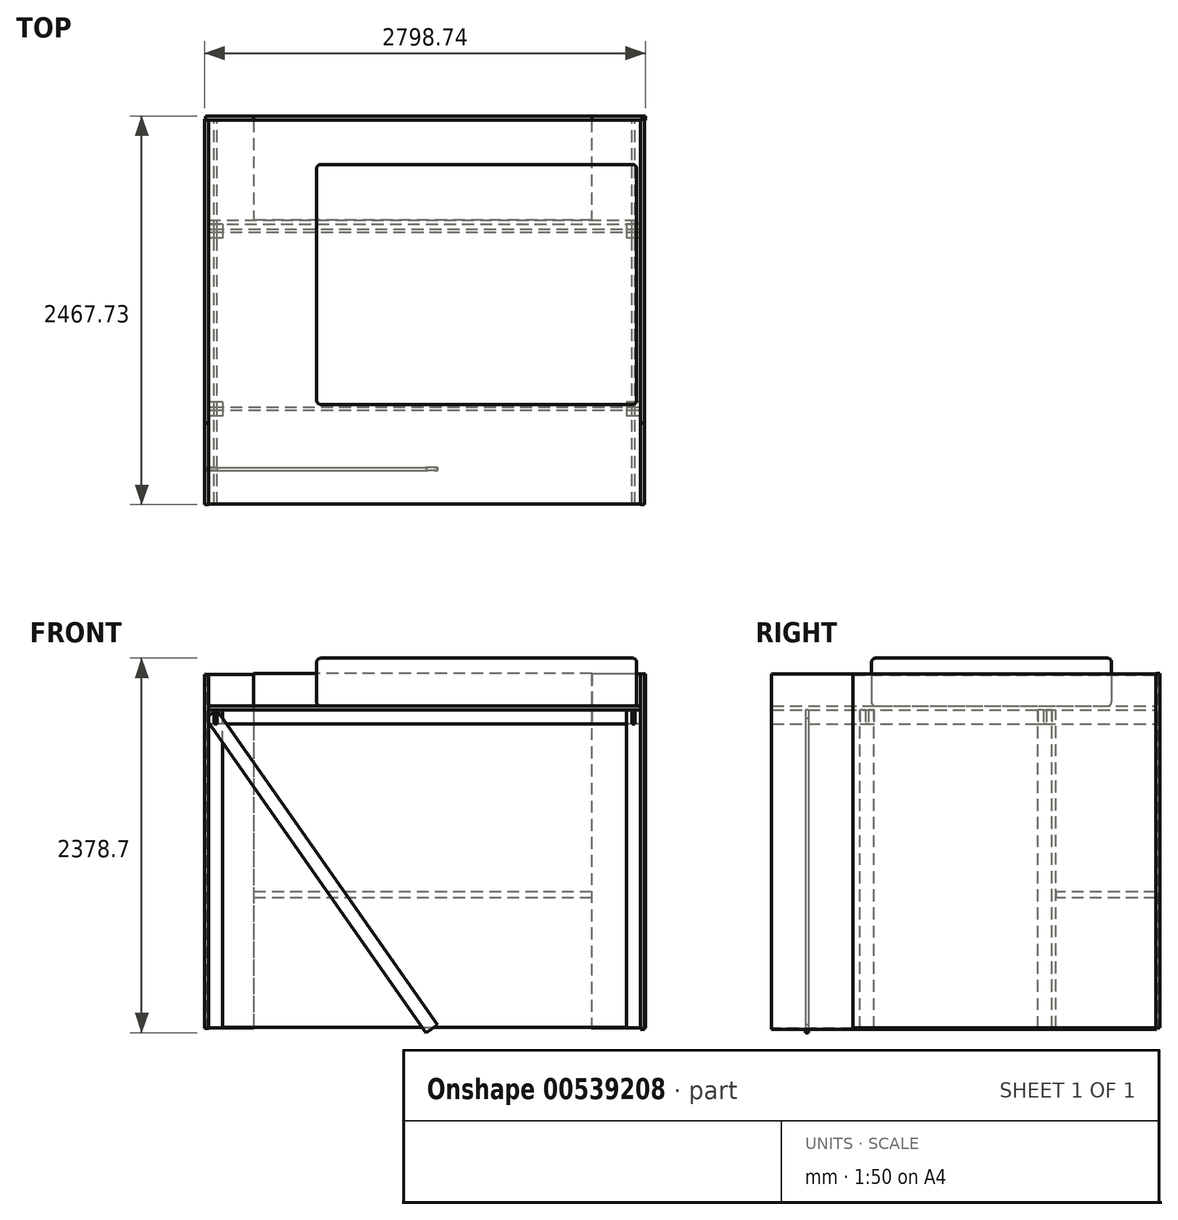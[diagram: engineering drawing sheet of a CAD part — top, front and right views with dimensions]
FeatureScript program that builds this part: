
annotation { "Feature Type Name" : "Feature", "Feature Type Description" : "" }
export const myFeature = defineFeature(function(context is Context, id is Id, definition is map)
    precondition{}
    {
        {
            var Q0;
            Q0=qCreatedBy(makeId("Top.planeOp"),FACE);
            var sketch = newSketch(context, id + "F0", { "sketchPlane" : qUnion([Q0])});
            skLineSegment(sketch, "E0.bottom", {"start": v(44.45, -44.45) * mm, "end": v(-44.45, -44.45) * mm});
            skLineSegment(sketch, "E0.top", {"start": v(44.45, 44.45) * mm, "end": v(-44.45, 44.45) * mm});
            skLineSegment(sketch, "E0.left", {"start": v(44.45, -44.45) * mm, "end": v(44.45, 44.45) * mm});
            skLineSegment(sketch, "E0.right", {"start": v(-44.45, -44.45) * mm, "end": v(-44.45, 44.45) * mm});
            skPoint(sketch, "E0.middle", {"position": v(0, 0) * mm});
            skSolve(sketch);
        }
        {
            var Q0;
            Q0=makeQuery(id+"F0.imprint","IMPRINT",FACE,{"disambiguationData":[TD([[makeQuery(id+"F0.imprint","IMPRINT",EDGE,{"derivedFrom":sQuery(id+"F0.wireOp",EDGE,"E0.bottom")}),-1.0]])]});
            extrude(context, id + "F1", {"entities" : qUnion([Q0]), "depth" : 2019.3 * mm, "offsetDistance" : 25.4 * mm});
        }
        {
            var Q0;
            Q0=qCreatedBy(makeId("Top.planeOp"),FACE);
            var sketch = newSketch(context, id + "F2", { "sketchPlane" : qUnion([Q0])});
            skLineSegment(sketch, "E1.bottom", {"start": v(9.53, 57.15) * mm, "end": v(-9.52, 57.15) * mm});
            skLineSegment(sketch, "E1.top", {"start": v(9.52, -57.15) * mm, "end": v(-9.53, -57.15) * mm});
            skLineSegment(sketch, "E1.left", {"start": v(9.53, 57.15) * mm, "end": v(9.52, -57.15) * mm});
            skLineSegment(sketch, "E1.right", {"start": v(-9.52, 57.15) * mm, "end": v(-9.53, -57.15) * mm});
            skPoint(sketch, "E1.middle", {"position": v(0, 0) * mm});
            skSolve(sketch);
        }
        {
            var Q0;
            Q0 = qSketchRegion(id + "F2", true);
            extrude(context, id + "F3", {"entities" : qUnion([Q0]), "operationType" : NewBodyOperationType.REMOVE, "oppositeDirection" : true, "depth" : -88.9 * mm, "offsetDistance" : 25.4 * mm});
        }
        {
            var Q0;
            Q0=qCreatedBy(makeId("Top.planeOp"),FACE);
            var sketch = newSketch(context, id + "F4", { "sketchPlane" : qUnion([Q0])});
            skLineSegment(sketch, "E2.bottom", {"start": v(58.89, 9.53) * mm, "end": v(-55.41, 9.52) * mm});
            skLineSegment(sketch, "E2.top", {"start": v(58.89, -9.52) * mm, "end": v(-55.41, -9.53) * mm});
            skLineSegment(sketch, "E2.left", {"start": v(58.89, 9.53) * mm, "end": v(58.89, -9.52) * mm});
            skLineSegment(sketch, "E2.right", {"start": v(-55.41, 9.52) * mm, "end": v(-55.41, -9.53) * mm});
            skPoint(sketch, "E2.middle", {"position": v(1.74, 0) * mm});
            skSolve(sketch);
        }
        {
            var Q0;
            Q0=makeQuery(id+"F4.imprint","IMPRINT",FACE,{"disambiguationData":[TD([[makeQuery(id+"F4.imprint","IMPRINT",EDGE,{"derivedFrom":sQuery(id+"F4.wireOp",EDGE,"E2.bottom")}),1.0]])]});
            extrude(context, id + "F5", {"entities" : qUnion([Q0]), "operationType" : NewBodyOperationType.REMOVE, "oppositeDirection" : true, "depth" : -88.9 * mm, "offsetDistance" : 25.4 * mm});
        }
        {
            var Q0;
            Q0=makeQuery(id+"F1.opExtrude","SWEPT_BODY",BODY,{"disambiguationData":[OSD([sQuery(id+"F0.wireOp",EDGE,"E0.bottom"),sQuery(id+"F0.wireOp",EDGE,"E0.top"),sQuery(id+"F0.wireOp",EDGE,"E0.left"),sQuery(id+"F0.wireOp",EDGE,"E0.right")])]});
            var Q1;
            Q1=sQuery(id+"F0.wireOp",EDGE,"E0.top");
            transform(context, id + "F6", {"entities" : qUnion([Q0]), "transformType" : TransformType.ROTATION, "transformAxis" : qUnion([Q1]), "angle" : 180 * degree, "makeCopy" : false});
        }
        {
            var Q0;
            Q0=makeQuery(id+"F1.opExtrude","SWEPT_BODY",BODY,{"disambiguationData":[OSD([sQuery(id+"F0.wireOp",EDGE,"E0.bottom"),sQuery(id+"F0.wireOp",EDGE,"E0.top"),sQuery(id+"F0.wireOp",EDGE,"E0.left"),sQuery(id+"F0.wireOp",EDGE,"E0.right")])]});
            var Q1;
            Q1=makeQuery(id+"F1.opExtrude","CAP_EDGE",EDGE,{"disambiguationData":[OSD([sQuery(id+"F0.wireOp",EDGE,"E0.top")])],"isStart":false});
            transform(context, id + "F7", {"entities" : qUnion([Q0]), "transformType" : TransformType.TRANSLATION_DISTANCE, "transformDirection" : qUnion([Q1]), "distance" : 914.4 * mm, "makeCopy" : false});
        }
        {
            var Q0;
            Q0=makeQuery(id+"F1.opExtrude","SWEPT_BODY",BODY,{"disambiguationData":[OSD([sQuery(id+"F0.wireOp",EDGE,"E0.bottom"),sQuery(id+"F0.wireOp",EDGE,"E0.top"),sQuery(id+"F0.wireOp",EDGE,"E0.left"),sQuery(id+"F0.wireOp",EDGE,"E0.right")])]});
            transform(context, id + "F8", {"entities" : qUnion([Q0]), "transformType" : TransformType.TRANSLATION_3D, "dx" : 1828.8 * mm, "dy" : 0 * mm, "dz" : 0 * mm, "makeCopy" : true});
        }
        {
            var Q0;
            Q0=makeQuery(id+"F1.opExtrude","SWEPT_BODY",BODY,{"disambiguationData":[OSD([sQuery(id+"F0.wireOp",EDGE,"E0.bottom"),sQuery(id+"F0.wireOp",EDGE,"E0.top"),sQuery(id+"F0.wireOp",EDGE,"E0.left"),sQuery(id+"F0.wireOp",EDGE,"E0.right")])]});
            var Q1;
            Q1=makeQuery(id+"F8.opPattern","COPY",BODY,{"derivedFrom":makeQuery(id+"F1.opExtrude","SWEPT_BODY",BODY,{"disambiguationData":[OSD([sQuery(id+"F0.wireOp",EDGE,"E0.bottom"),sQuery(id+"F0.wireOp",EDGE,"E0.top"),sQuery(id+"F0.wireOp",EDGE,"E0.left"),sQuery(id+"F0.wireOp",EDGE,"E0.right")])]}),"instanceName":"1"});
            transform(context, id + "F9", {"entities" : qUnion([Q0, Q1]), "transformType" : TransformType.TRANSLATION_3D, "dx" : 0 * mm, "dy" : 762 * mm, "dz" : 0 * mm, "makeCopy" : false});
        }
        {
            var Q0;
            Q0=makeQuery(id+"F8.opPattern","COPY",BODY,{"derivedFrom":makeQuery(id+"F1.opExtrude","SWEPT_BODY",BODY,{"disambiguationData":[OSD([sQuery(id+"F0.wireOp",EDGE,"E0.bottom"),sQuery(id+"F0.wireOp",EDGE,"E0.top"),sQuery(id+"F0.wireOp",EDGE,"E0.left"),sQuery(id+"F0.wireOp",EDGE,"E0.right")])]}),"instanceName":"1"});
            transform(context, id + "F10", {"entities" : qUnion([Q0]), "transformType" : TransformType.TRANSLATION_3D, "dx" : 0 * mm, "dy" : -1524 * mm, "dz" : 0 * mm, "makeCopy" : true});
        }
        {
            var Q0;
            Q0=makeQuery(id+"F1.opExtrude","SWEPT_BODY",BODY,{"disambiguationData":[OSD([sQuery(id+"F0.wireOp",EDGE,"E0.bottom"),sQuery(id+"F0.wireOp",EDGE,"E0.top"),sQuery(id+"F0.wireOp",EDGE,"E0.left"),sQuery(id+"F0.wireOp",EDGE,"E0.right")])]});
            transform(context, id + "F11", {"entities" : qUnion([Q0]), "transformType" : TransformType.TRANSLATION_3D, "dx" : 0 * mm, "dy" : -1524 * mm, "dz" : 0 * mm, "makeCopy" : true});
        }
        {
            var Q0;
            Q0=qCreatedBy(makeId("Top.planeOp"),FACE);
            var sketch = newSketch(context, id + "F12", { "sketchPlane" : qUnion([Q0])});
            skLineSegment(sketch, "E3.bottom", {"start": v(-1219.2, -1371.6) * mm, "end": v(1219.2, -1371.6) * mm});
            skLineSegment(sketch, "E3.top", {"start": v(-1219.2, 1371.6) * mm, "end": v(1219.2, 1371.6) * mm});
            skLineSegment(sketch, "E3.left", {"start": v(-1219.2, -1371.6) * mm, "end": v(-1219.2, 1371.6) * mm});
            skLineSegment(sketch, "E3.right", {"start": v(1219.2, -1371.6) * mm, "end": v(1219.2, 1371.6) * mm});
            skPoint(sketch, "E3.middle", {"position": v(0, 0) * mm});
            skSolve(sketch);
        }
        {
            var Q0;
            Q0=makeQuery(id+"F12.imprint","IMPRINT",FACE,{"disambiguationData":[TD([[makeQuery(id+"F12.imprint","IMPRINT",EDGE,{"derivedFrom":sQuery(id+"F12.wireOp",EDGE,"E3.bottom")}),1.0]])]});
            extrude(context, id + "F13", {"entities" : qUnion([Q0]), "depth" : 25.4 * mm, "offsetDistance" : 25.4 * mm});
        }
        {
            var Q0;
            Q0=makeQuery(id+"F13.opExtrude","SWEPT_BODY",BODY,{"disambiguationData":[OSD([sQuery(id+"F12.wireOp",EDGE,"E3.bottom"),sQuery(id+"F12.wireOp",EDGE,"E3.top"),sQuery(id+"F12.wireOp",EDGE,"E3.left"),sQuery(id+"F12.wireOp",EDGE,"E3.right")])]});
            var Q1;
            Q1=makeQuery(id+"F11.opPattern","COPY",EDGE,{"derivedFrom":makeQuery(id+"F1.opExtrude","SWEPT_EDGE",EDGE,{"disambiguationData":[OSD([sQuery(id+"F0.wireOp",EDGE,"E0.top"),sQuery(id+"F0.wireOp",EDGE,"E0.right")])]}),"instanceName":"1"});
            transform(context, id + "F14", {"entities" : qUnion([Q0]), "transformType" : TransformType.ROTATION, "transformAxis" : qUnion([Q1]), "angle" : 90 * degree, "makeCopy" : false});
        }
        {
            var Q0;
            Q0=makeQuery(id+"F13.opExtrude","SWEPT_BODY",BODY,{"disambiguationData":[OSD([sQuery(id+"F12.wireOp",EDGE,"E3.bottom"),sQuery(id+"F12.wireOp",EDGE,"E3.top"),sQuery(id+"F12.wireOp",EDGE,"E3.left"),sQuery(id+"F12.wireOp",EDGE,"E3.right")])]});
            transform(context, id + "F15", {"entities" : qUnion([Q0]), "transformType" : TransformType.TRANSLATION_3D, "dx" : 1625.6 * mm, "dy" : -76.2 * mm, "dz" : 0 * mm, "makeCopy" : false});
        }
        {
            var Q0;
            Q0=makeQuery(id+"F11.opPattern","COPY",BODY,{"derivedFrom":makeQuery(id+"F1.opExtrude","SWEPT_BODY",BODY,{"disambiguationData":[OSD([sQuery(id+"F0.wireOp",EDGE,"E0.bottom"),sQuery(id+"F0.wireOp",EDGE,"E0.top"),sQuery(id+"F0.wireOp",EDGE,"E0.left"),sQuery(id+"F0.wireOp",EDGE,"E0.right")])]}),"instanceName":"1"});
            transform(context, id + "F16", {"entities" : qUnion([Q0]), "transformType" : TransformType.TRANSLATION_3D, "dx" : -196.85 * mm, "dy" : 0 * mm, "dz" : 0 * mm, "makeCopy" : false});
        }
        {
            var Q0;
            Q0=makeQuery(id+"F1.opExtrude","SWEPT_BODY",BODY,{"disambiguationData":[OSD([sQuery(id+"F0.wireOp",EDGE,"E0.bottom"),sQuery(id+"F0.wireOp",EDGE,"E0.top"),sQuery(id+"F0.wireOp",EDGE,"E0.left"),sQuery(id+"F0.wireOp",EDGE,"E0.right")])]});
            transform(context, id + "F17", {"entities" : qUnion([Q0]), "transformType" : TransformType.TRANSLATION_3D, "dx" : -196.85 * mm, "dy" : 0 * mm, "dz" : 0 * mm, "makeCopy" : false});
        }
        {
            var Q0;
            Q0=makeQuery(id+"F8.opPattern","COPY",BODY,{"derivedFrom":makeQuery(id+"F1.opExtrude","SWEPT_BODY",BODY,{"disambiguationData":[OSD([sQuery(id+"F0.wireOp",EDGE,"E0.bottom"),sQuery(id+"F0.wireOp",EDGE,"E0.top"),sQuery(id+"F0.wireOp",EDGE,"E0.left"),sQuery(id+"F0.wireOp",EDGE,"E0.right")])]}),"instanceName":"1"});
            var Q1;
            Q1=makeQuery(id+"F10.opPattern","COPY",BODY,{"derivedFrom":makeQuery(id+"F8.opPattern","COPY",BODY,{"derivedFrom":makeQuery(id+"F1.opExtrude","SWEPT_BODY",BODY,{"disambiguationData":[OSD([sQuery(id+"F0.wireOp",EDGE,"E0.bottom"),sQuery(id+"F0.wireOp",EDGE,"E0.top"),sQuery(id+"F0.wireOp",EDGE,"E0.left"),sQuery(id+"F0.wireOp",EDGE,"E0.right")])]}),"instanceName":"1"}),"instanceName":"1"});
            transform(context, id + "F18", {"entities" : qUnion([Q0, Q1]), "transformType" : TransformType.TRANSLATION_3D, "dx" : 196.85 * mm, "dy" : 0 * mm, "dz" : 0 * mm, "makeCopy" : false});
        }
        {
            var Q0;
            Q0=makeQuery(id+"F13.opExtrude","SWEPT_BODY",BODY,{"disambiguationData":[OSD([sQuery(id+"F12.wireOp",EDGE,"E3.bottom"),sQuery(id+"F12.wireOp",EDGE,"E3.top"),sQuery(id+"F12.wireOp",EDGE,"E3.left"),sQuery(id+"F12.wireOp",EDGE,"E3.right")])]});
            transform(context, id + "F19", {"entities" : qUnion([Q0]), "transformType" : TransformType.TRANSLATION_3D, "dx" : 63.5 * mm, "dy" : 0 * mm, "dz" : 0 * mm, "makeCopy" : false});
        }
        {
            var Q0;
            Q0=makeQuery(id+"F13.opExtrude","SWEPT_BODY",BODY,{"disambiguationData":[OSD([sQuery(id+"F12.wireOp",EDGE,"E3.bottom"),sQuery(id+"F12.wireOp",EDGE,"E3.top"),sQuery(id+"F12.wireOp",EDGE,"E3.left"),sQuery(id+"F12.wireOp",EDGE,"E3.right")])]});
            transform(context, id + "F20", {"entities" : qUnion([Q0]), "transformType" : TransformType.TRANSLATION_3D, "dx" : 0 * mm, "dy" : -50.8 * mm, "dz" : 0 * mm, "makeCopy" : false});
        }
        {
            var Q0;
            Q0=makeQuery(id+"F1.opExtrude","SWEPT_BODY",BODY,{"disambiguationData":[OSD([sQuery(id+"F0.wireOp",EDGE,"E0.bottom"),sQuery(id+"F0.wireOp",EDGE,"E0.top"),sQuery(id+"F0.wireOp",EDGE,"E0.left"),sQuery(id+"F0.wireOp",EDGE,"E0.right")])]});
            var Q1;
            Q1=makeQuery(id+"F11.opPattern","COPY",BODY,{"derivedFrom":makeQuery(id+"F1.opExtrude","SWEPT_BODY",BODY,{"disambiguationData":[OSD([sQuery(id+"F0.wireOp",EDGE,"E0.bottom"),sQuery(id+"F0.wireOp",EDGE,"E0.top"),sQuery(id+"F0.wireOp",EDGE,"E0.left"),sQuery(id+"F0.wireOp",EDGE,"E0.right")])]}),"instanceName":"1"});
            transform(context, id + "F21", {"entities" : qUnion([Q0, Q1]), "transformType" : TransformType.TRANSLATION_3D, "dx" : -6.35 * mm, "dy" : 0 * mm, "dz" : 0 * mm, "makeCopy" : false});
        }
        {
            var Q0;
            Q0=makeQuery(id+"F8.opPattern","COPY",BODY,{"derivedFrom":makeQuery(id+"F1.opExtrude","SWEPT_BODY",BODY,{"disambiguationData":[OSD([sQuery(id+"F0.wireOp",EDGE,"E0.bottom"),sQuery(id+"F0.wireOp",EDGE,"E0.top"),sQuery(id+"F0.wireOp",EDGE,"E0.left"),sQuery(id+"F0.wireOp",EDGE,"E0.right")])]}),"instanceName":"1"});
            var Q1;
            Q1=makeQuery(id+"F10.opPattern","COPY",BODY,{"derivedFrom":makeQuery(id+"F8.opPattern","COPY",BODY,{"derivedFrom":makeQuery(id+"F1.opExtrude","SWEPT_BODY",BODY,{"disambiguationData":[OSD([sQuery(id+"F0.wireOp",EDGE,"E0.bottom"),sQuery(id+"F0.wireOp",EDGE,"E0.top"),sQuery(id+"F0.wireOp",EDGE,"E0.left"),sQuery(id+"F0.wireOp",EDGE,"E0.right")])]}),"instanceName":"1"}),"instanceName":"1"});
            transform(context, id + "F22", {"entities" : qUnion([Q0, Q1]), "transformType" : TransformType.TRANSLATION_3D, "dx" : 6.35 * mm, "dy" : 0 * mm, "dz" : 0 * mm, "makeCopy" : false});
        }
        {
            var Q0;
            Q0=qCreatedBy(makeId("Top.planeOp"),FACE);
            var sketch = newSketch(context, id + "F23", { "sketchPlane" : qUnion([Q0])});
            skLineSegment(sketch, "E4.bottom", {"start": v(1073.15, 317.5) * mm, "end": v(-1073.15, 317.5) * mm});
            skLineSegment(sketch, "E4.top", {"start": v(1073.15, -317.5) * mm, "end": v(-1073.15, -317.5) * mm});
            skLineSegment(sketch, "E4.left", {"start": v(1073.15, 317.5) * mm, "end": v(1073.15, -317.5) * mm});
            skLineSegment(sketch, "E4.right", {"start": v(-1073.15, 317.5) * mm, "end": v(-1073.15, -317.5) * mm});
            skPoint(sketch, "E4.middle", {"position": v(0, 0) * mm});
            skSolve(sketch);
        }
        {
            var Q0;
            Q0=makeQuery(id+"F23.imprint","IMPRINT",FACE,{"disambiguationData":[TD([[makeQuery(id+"F23.imprint","IMPRINT",EDGE,{"derivedFrom":sQuery(id+"F23.wireOp",EDGE,"E4.bottom")}),1.0]])]});
            extrude(context, id + "F24", {"entities" : qUnion([Q0]), "depth" : 38.1 * mm, "offsetDistance" : 25.4 * mm});
        }
        {
            var Q0;
            Q0=makeQuery(id+"F24.opExtrude","SWEPT_BODY",BODY,{"disambiguationData":[OSD([sQuery(id+"F23.wireOp",EDGE,"E4.bottom"),sQuery(id+"F23.wireOp",EDGE,"E4.top"),sQuery(id+"F23.wireOp",EDGE,"E4.left"),sQuery(id+"F23.wireOp",EDGE,"E4.right")])]});
            transform(context, id + "F25", {"entities" : qUnion([Q0]), "transformType" : TransformType.TRANSLATION_3D, "dx" : 0 * mm, "dy" : 0 * mm, "dz" : -1193.8 * mm, "makeCopy" : false});
        }
        {
            var Q0;
            Q0=makeQuery(id+"F24.opExtrude","SWEPT_BODY",BODY,{"disambiguationData":[OSD([sQuery(id+"F23.wireOp",EDGE,"E4.bottom"),sQuery(id+"F23.wireOp",EDGE,"E4.top"),sQuery(id+"F23.wireOp",EDGE,"E4.left"),sQuery(id+"F23.wireOp",EDGE,"E4.right")])]});
            transform(context, id + "F26", {"entities" : qUnion([Q0]), "transformType" : TransformType.TRANSLATION_3D, "dx" : 0 * mm, "dy" : 1016 * mm, "dz" : 0 * mm, "makeCopy" : false});
        }
        {
            var Q0;
            Q0=qCreatedBy(makeId("Front.planeOp"),FACE);
            var sketch = newSketch(context, id + "F27", { "sketchPlane" : qUnion([Q0])});
            skLineSegment(sketch, "E5.bottom", {"start": v(-1261, -20.47) * mm, "end": v(-1241.95, -20.47) * mm});
            skLineSegment(sketch, "E5.top", {"start": v(-1261, -109.37) * mm, "end": v(-1241.95, -109.37) * mm});
            skLineSegment(sketch, "E5.left", {"start": v(-1261, -20.47) * mm, "end": v(-1261, -109.37) * mm});
            skLineSegment(sketch, "E5.right", {"start": v(-1241.95, -20.47) * mm, "end": v(-1241.95, -109.37) * mm});
            skSolve(sketch);
        }
        {
            var Q0;
            Q0 = qSketchRegion(id + "F27", true);
            extrude(context, id + "F28", {"entities" : qUnion([Q0]), "depth" : 2438.4 * mm, "offsetDistance" : 25.4 * mm});
        }
        {
            var Q0;
            Q0=makeQuery(id+"F28.opExtrude","SWEPT_BODY",BODY,{"disambiguationData":[OSD([sQuery(id+"F27.wireOp",EDGE,"E5.bottom"),sQuery(id+"F27.wireOp",EDGE,"E5.top"),sQuery(id+"F27.wireOp",EDGE,"E5.left"),sQuery(id+"F27.wireOp",EDGE,"E5.right")])]});
            transform(context, id + "F29", {"entities" : qUnion([Q0]), "transformType" : TransformType.TRANSLATION_3D, "dx" : 0 * mm, "dy" : 1219.2 * mm, "dz" : 0 * mm, "makeCopy" : false});
        }
        {
            var Q0;
            Q0=makeQuery(id+"F28.opExtrude","SWEPT_BODY",BODY,{"disambiguationData":[OSD([sQuery(id+"F27.wireOp",EDGE,"E5.bottom"),sQuery(id+"F27.wireOp",EDGE,"E5.top"),sQuery(id+"F27.wireOp",EDGE,"E5.left"),sQuery(id+"F27.wireOp",EDGE,"E5.right")])]});
            transform(context, id + "F30", {"entities" : qUnion([Q0]), "transformType" : TransformType.TRANSLATION_3D, "dx" : 0 * mm, "dy" : 114.3 * mm, "dz" : 0 * mm, "makeCopy" : false});
        }
        {
            var Q0;
            Q0=makeQuery(id+"F28.opExtrude","SWEPT_BODY",BODY,{"disambiguationData":[OSD([sQuery(id+"F27.wireOp",EDGE,"E5.bottom"),sQuery(id+"F27.wireOp",EDGE,"E5.top"),sQuery(id+"F27.wireOp",EDGE,"E5.left"),sQuery(id+"F27.wireOp",EDGE,"E5.right")])]});
            transform(context, id + "F31", {"entities" : qUnion([Q0]), "transformType" : TransformType.TRANSLATION_3D, "dx" : 0 * mm, "dy" : 0 * mm, "dz" : 20.32 * mm, "makeCopy" : false});
        }
        {
            var Q0;
            Q0=makeQuery(id+"F28.opExtrude","SWEPT_BODY",BODY,{"disambiguationData":[OSD([sQuery(id+"F27.wireOp",EDGE,"E5.bottom"),sQuery(id+"F27.wireOp",EDGE,"E5.top"),sQuery(id+"F27.wireOp",EDGE,"E5.left"),sQuery(id+"F27.wireOp",EDGE,"E5.right")])]});
            transform(context, id + "F32", {"entities" : qUnion([Q0]), "transformType" : TransformType.TRANSLATION_3D, "dx" : 133.88 * mm, "dy" : 0 * mm, "dz" : 0 * mm, "makeCopy" : false});
        }
        {
            var Q0;
            Q0=makeQuery(id+"F28.opExtrude","SWEPT_BODY",BODY,{"disambiguationData":[OSD([sQuery(id+"F27.wireOp",EDGE,"E5.bottom"),sQuery(id+"F27.wireOp",EDGE,"E5.top"),sQuery(id+"F27.wireOp",EDGE,"E5.left"),sQuery(id+"F27.wireOp",EDGE,"E5.right")])]});
            transform(context, id + "F33", {"entities" : qUnion([Q0]), "transformType" : TransformType.TRANSLATION_3D, "dx" : 2235.2 * mm, "dy" : 0 * mm, "dz" : 0 * mm, "makeCopy" : true});
        }
        {
            var Q0;
            Q0=makeQuery(id+"F33.opPattern","COPY",BODY,{"derivedFrom":makeQuery(id+"F28.opExtrude","SWEPT_BODY",BODY,{"disambiguationData":[OSD([sQuery(id+"F27.wireOp",EDGE,"E5.bottom"),sQuery(id+"F27.wireOp",EDGE,"E5.top"),sQuery(id+"F27.wireOp",EDGE,"E5.left"),sQuery(id+"F27.wireOp",EDGE,"E5.right")])]}),"instanceName":"1"});
            deleteBodies(context, id + "F34", {"entities" : qUnion([Q0])});
        }
        {
            var Q0;
            Q0=makeQuery(id+"F28.opExtrude","SWEPT_BODY",BODY,{"disambiguationData":[OSD([sQuery(id+"F27.wireOp",EDGE,"E5.bottom"),sQuery(id+"F27.wireOp",EDGE,"E5.top"),sQuery(id+"F27.wireOp",EDGE,"E5.left"),sQuery(id+"F27.wireOp",EDGE,"E5.right")])]});
            var Q1;
            Q1=qCreatedBy(makeId("Right.planeOp"),FACE);
            mirror(context, id + "F35", {"entities" : qUnion([Q0]), "mirrorPlane" : qUnion([Q1])});
        }
        {
            var Q0;
            Q0=qCreatedBy(makeId("Right.planeOp"),FACE);
            var sketch = newSketch(context, id + "F36", { "sketchPlane" : qUnion([Q0])});
            skLineSegment(sketch, "E6.bottom", {"start": v(840.89, 0) * mm, "end": v(859.94, 0) * mm});
            skLineSegment(sketch, "E6.top", {"start": v(840.89, -88.9) * mm, "end": v(859.94, -88.9) * mm});
            skLineSegment(sketch, "E6.left", {"start": v(840.89, 0) * mm, "end": v(840.89, -88.9) * mm});
            skLineSegment(sketch, "E6.right", {"start": v(859.94, 0) * mm, "end": v(859.94, -88.9) * mm});
            skSolve(sketch);
        }
        {
            var Q0;
            Q0 = qSketchRegion(id + "F36", true);
            extrude(context, id + "F37", {"entities" : qUnion([Q0]), "depth" : 2743.2 * mm, "offsetDistance" : 25.4 * mm});
        }
        {
            var Q0;
            Q0=makeQuery(id+"F37.opExtrude","SWEPT_BODY",BODY,{"disambiguationData":[OSD([sQuery(id+"F36.wireOp",EDGE,"E6.bottom"),sQuery(id+"F36.wireOp",EDGE,"E6.top"),sQuery(id+"F36.wireOp",EDGE,"E6.left"),sQuery(id+"F36.wireOp",EDGE,"E6.right")])]});
            transform(context, id + "F38", {"entities" : qUnion([Q0]), "transformType" : TransformType.TRANSLATION_3D, "dx" : -1358.9 * mm, "dy" : 0 * mm, "dz" : 0 * mm, "makeCopy" : false});
        }
        {
            var Q0;
            Q0=makeQuery(id+"F37.opExtrude","SWEPT_BODY",BODY,{"disambiguationData":[OSD([sQuery(id+"F36.wireOp",EDGE,"E6.bottom"),sQuery(id+"F36.wireOp",EDGE,"E6.top"),sQuery(id+"F36.wireOp",EDGE,"E6.left"),sQuery(id+"F36.wireOp",EDGE,"E6.right")])]});
            transform(context, id + "F39", {"entities" : qUnion([Q0]), "transformType" : TransformType.TRANSLATION_3D, "dx" : 0 * mm, "dy" : -1523.5 * mm, "dz" : 0 * mm, "makeCopy" : true});
        }
        {
            var Q0;
            Q0=makeQuery(id+"F28.opExtrude","SWEPT_BODY",BODY,{"disambiguationData":[OSD([sQuery(id+"F27.wireOp",EDGE,"E5.bottom"),sQuery(id+"F27.wireOp",EDGE,"E5.top"),sQuery(id+"F27.wireOp",EDGE,"E5.left"),sQuery(id+"F27.wireOp",EDGE,"E5.right")])]});
            transform(context, id + "F40", {"entities" : qUnion([Q0]), "transformType" : TransformType.TRANSLATION_3D, "dx" : -330.2 * mm, "dy" : 0 * mm, "dz" : 0 * mm, "makeCopy" : true});
        }
        {
            var Q0;
            Q0=makeQuery(id+"F40.opPattern","COPY",BODY,{"derivedFrom":makeQuery(id+"F28.opExtrude","SWEPT_BODY",BODY,{"disambiguationData":[OSD([sQuery(id+"F27.wireOp",EDGE,"E5.bottom"),sQuery(id+"F27.wireOp",EDGE,"E5.top"),sQuery(id+"F27.wireOp",EDGE,"E5.left"),sQuery(id+"F27.wireOp",EDGE,"E5.right")])]}),"instanceName":"1"});
            transform(context, id + "F41", {"entities" : qUnion([Q0]), "transformType" : TransformType.TRANSLATION_3D, "dx" : 0 * mm, "dy" : 422.27 * mm, "dz" : 0 * mm, "makeCopy" : false});
        }
        {
            var Q0;
            Q0=makeQuery(id+"F40.opPattern","COPY",BODY,{"derivedFrom":makeQuery(id+"F28.opExtrude","SWEPT_BODY",BODY,{"disambiguationData":[OSD([sQuery(id+"F27.wireOp",EDGE,"E5.bottom"),sQuery(id+"F27.wireOp",EDGE,"E5.top"),sQuery(id+"F27.wireOp",EDGE,"E5.left"),sQuery(id+"F27.wireOp",EDGE,"E5.right")])]}),"instanceName":"1"});
            var Q1;
            {var subQ0=sQuery(id+"F36.wireOp",EDGE,"E6.left");var subQ1=sQuery(id+"F36.wireOp",EDGE,"E6.bottom");Q1=makeQuery(id+"F71cGU53pQJ6Zgx_5.boolean.opBoolean","MERGE",EDGE,{"derivedFrom":[makeQuery(id+"F39.opPattern","COPY",EDGE,{"derivedFrom":makeQuery(id+"F37.opExtrude","SWEPT_EDGE",EDGE,{"disambiguationData":[OSD([subQ1,subQ0])]}),"instanceName":"1"}),makeQuery(id+"F71cGU53pQJ6Zgx_5.opExtrude","SWEPT_EDGE",EDGE,{"disambiguationData":[OSD([subQ1,subQ0])]})]});}
            transform(context, id + "F42", {"entities" : qUnion([Q0]), "transformType" : TransformType.ROTATION, "transformAxis" : qUnion([Q1]), "angle" : 55 * degree, "makeCopy" : false});
        }
        {
            var Q0;
            Q0=makeQuery(id+"F40.opPattern","COPY",BODY,{"derivedFrom":makeQuery(id+"F28.opExtrude","SWEPT_BODY",BODY,{"disambiguationData":[OSD([sQuery(id+"F27.wireOp",EDGE,"E5.bottom"),sQuery(id+"F27.wireOp",EDGE,"E5.top"),sQuery(id+"F27.wireOp",EDGE,"E5.left"),sQuery(id+"F27.wireOp",EDGE,"E5.right")])]}),"instanceName":"1"});
            var Q1;
            Q1=makeQuery(id+"F39.opPattern","COPY",BODY,{"derivedFrom":makeQuery(id+"F37.opExtrude","SWEPT_BODY",BODY,{"disambiguationData":[OSD([sQuery(id+"F36.wireOp",EDGE,"E6.bottom"),sQuery(id+"F36.wireOp",EDGE,"E6.top"),sQuery(id+"F36.wireOp",EDGE,"E6.left"),sQuery(id+"F36.wireOp",EDGE,"E6.right")])]}),"instanceName":"1"});
            var Q2;
            Q2=makeQuery(id+"F11.opPattern","COPY",BODY,{"derivedFrom":makeQuery(id+"F1.opExtrude","SWEPT_BODY",BODY,{"disambiguationData":[OSD([sQuery(id+"F0.wireOp",EDGE,"E0.bottom"),sQuery(id+"F0.wireOp",EDGE,"E0.top"),sQuery(id+"F0.wireOp",EDGE,"E0.left"),sQuery(id+"F0.wireOp",EDGE,"E0.right")])]}),"instanceName":"1"});
            var Q3;
            Q3=makeQuery(id+"F10.opPattern","COPY",BODY,{"derivedFrom":makeQuery(id+"F8.opPattern","COPY",BODY,{"derivedFrom":makeQuery(id+"F1.opExtrude","SWEPT_BODY",BODY,{"disambiguationData":[OSD([sQuery(id+"F0.wireOp",EDGE,"E0.bottom"),sQuery(id+"F0.wireOp",EDGE,"E0.top"),sQuery(id+"F0.wireOp",EDGE,"E0.left"),sQuery(id+"F0.wireOp",EDGE,"E0.right")])]}),"instanceName":"1"}),"instanceName":"1"});
            transform(context, id + "F43", {"entities" : qUnion([Q0, Q1, Q2, Q3]), "transformType" : TransformType.TRANSLATION_3D, "dx" : 0 * mm, "dy" : 558.8 * mm, "dz" : 0 * mm, "makeCopy" : false});
        }
        {
            var Q0;
            Q0=makeQuery(id+"F11.opPattern","COPY",BODY,{"derivedFrom":makeQuery(id+"F1.opExtrude","SWEPT_BODY",BODY,{"disambiguationData":[OSD([sQuery(id+"F0.wireOp",EDGE,"E0.bottom"),sQuery(id+"F0.wireOp",EDGE,"E0.top"),sQuery(id+"F0.wireOp",EDGE,"E0.left"),sQuery(id+"F0.wireOp",EDGE,"E0.right")])]}),"instanceName":"1"});
            transform(context, id + "F44", {"entities" : qUnion([Q0]), "transformType" : TransformType.TRANSLATION_3D, "dx" : 0 * mm, "dy" : -946.15 * mm, "dz" : 0 * mm, "makeCopy" : true});
        }
        {
            var Q0;
            Q0=makeQuery(id+"F10.opPattern","COPY",BODY,{"derivedFrom":makeQuery(id+"F8.opPattern","COPY",BODY,{"derivedFrom":makeQuery(id+"F1.opExtrude","SWEPT_BODY",BODY,{"disambiguationData":[OSD([sQuery(id+"F0.wireOp",EDGE,"E0.bottom"),sQuery(id+"F0.wireOp",EDGE,"E0.top"),sQuery(id+"F0.wireOp",EDGE,"E0.left"),sQuery(id+"F0.wireOp",EDGE,"E0.right")])]}),"instanceName":"1"}),"instanceName":"1"});
            transform(context, id + "F45", {"entities" : qUnion([Q0]), "transformType" : TransformType.TRANSLATION_3D, "dx" : 0 * mm, "dy" : -946.15 * mm, "dz" : 0 * mm, "makeCopy" : true});
        }
        {
            var Q0;
            Q0=makeQuery(id+"F37.opExtrude","SWEPT_BODY",BODY,{"disambiguationData":[OSD([sQuery(id+"F36.wireOp",EDGE,"E6.bottom"),sQuery(id+"F36.wireOp",EDGE,"E6.top"),sQuery(id+"F36.wireOp",EDGE,"E6.left"),sQuery(id+"F36.wireOp",EDGE,"E6.right")])]});
            transform(context, id + "F46", {"entities" : qUnion([Q0]), "transformType" : TransformType.TRANSLATION_3D, "dx" : 0 * mm, "dy" : -1910.86 * mm, "dz" : 0 * mm, "makeCopy" : true});
        }
        {
            var Q0;
            Q0=makeQuery(id+"F40.opPattern","COPY",BODY,{"derivedFrom":makeQuery(id+"F28.opExtrude","SWEPT_BODY",BODY,{"disambiguationData":[OSD([sQuery(id+"F27.wireOp",EDGE,"E5.bottom"),sQuery(id+"F27.wireOp",EDGE,"E5.top"),sQuery(id+"F27.wireOp",EDGE,"E5.left"),sQuery(id+"F27.wireOp",EDGE,"E5.right")])]}),"instanceName":"1"});
            var Q1;
            Q1=makeQuery(id+"F10.opPattern","COPY",BODY,{"derivedFrom":makeQuery(id+"F8.opPattern","COPY",BODY,{"derivedFrom":makeQuery(id+"F1.opExtrude","SWEPT_BODY",BODY,{"disambiguationData":[OSD([sQuery(id+"F0.wireOp",EDGE,"E0.bottom"),sQuery(id+"F0.wireOp",EDGE,"E0.top"),sQuery(id+"F0.wireOp",EDGE,"E0.left"),sQuery(id+"F0.wireOp",EDGE,"E0.right")])]}),"instanceName":"1"}),"instanceName":"1"});
            var Q2;
            Q2=makeQuery(id+"F11.opPattern","COPY",BODY,{"derivedFrom":makeQuery(id+"F1.opExtrude","SWEPT_BODY",BODY,{"disambiguationData":[OSD([sQuery(id+"F0.wireOp",EDGE,"E0.bottom"),sQuery(id+"F0.wireOp",EDGE,"E0.top"),sQuery(id+"F0.wireOp",EDGE,"E0.left"),sQuery(id+"F0.wireOp",EDGE,"E0.right")])]}),"instanceName":"1"});
            var Q3;
            Q3=makeQuery(id+"F39.opPattern","COPY",BODY,{"derivedFrom":makeQuery(id+"F37.opExtrude","SWEPT_BODY",BODY,{"disambiguationData":[OSD([sQuery(id+"F36.wireOp",EDGE,"E6.bottom"),sQuery(id+"F36.wireOp",EDGE,"E6.top"),sQuery(id+"F36.wireOp",EDGE,"E6.left"),sQuery(id+"F36.wireOp",EDGE,"E6.right")])]}),"instanceName":"1"});
            transform(context, id + "F47", {"entities" : qUnion([Q0, Q1, Q2, Q3]), "transformType" : TransformType.TRANSLATION_3D, "dx" : 0 * mm, "dy" : -387.35 * mm, "dz" : 0 * mm, "makeCopy" : false});
        }
        {
            var Q0;
            Q0=makeQuery(id+"F46.opPattern","COPY",BODY,{"derivedFrom":makeQuery(id+"F37.opExtrude","SWEPT_BODY",BODY,{"disambiguationData":[OSD([sQuery(id+"F36.wireOp",EDGE,"E6.bottom"),sQuery(id+"F36.wireOp",EDGE,"E6.top"),sQuery(id+"F36.wireOp",EDGE,"E6.left"),sQuery(id+"F36.wireOp",EDGE,"E6.right")])]}),"instanceName":"1"});
            deleteBodies(context, id + "F48", {"entities" : qUnion([Q0])});
        }
        {
            var Q0;
            Q0=makeQuery(id+"F45.opPattern","COPY",BODY,{"derivedFrom":makeQuery(id+"F10.opPattern","COPY",BODY,{"derivedFrom":makeQuery(id+"F8.opPattern","COPY",BODY,{"derivedFrom":makeQuery(id+"F1.opExtrude","SWEPT_BODY",BODY,{"disambiguationData":[OSD([sQuery(id+"F0.wireOp",EDGE,"E0.bottom"),sQuery(id+"F0.wireOp",EDGE,"E0.top"),sQuery(id+"F0.wireOp",EDGE,"E0.left"),sQuery(id+"F0.wireOp",EDGE,"E0.right")])]}),"instanceName":"1"}),"instanceName":"1"}),"instanceName":"1"});
            deleteBodies(context, id + "F49", {"entities" : qUnion([Q0])});
        }
        {
            var Q0;
            Q0=makeQuery(id+"F44.opPattern","COPY",BODY,{"derivedFrom":makeQuery(id+"F11.opPattern","COPY",BODY,{"derivedFrom":makeQuery(id+"F1.opExtrude","SWEPT_BODY",BODY,{"disambiguationData":[OSD([sQuery(id+"F0.wireOp",EDGE,"E0.bottom"),sQuery(id+"F0.wireOp",EDGE,"E0.top"),sQuery(id+"F0.wireOp",EDGE,"E0.left"),sQuery(id+"F0.wireOp",EDGE,"E0.right")])]}),"instanceName":"1"}),"instanceName":"1"});
            deleteBodies(context, id + "F50", {"entities" : qUnion([Q0])});
        }
        {
            var Q0;
            Q0=makeQuery(id+"F13.opExtrude","SWEPT_FACE",FACE,{"disambiguationData":[OSD([sQuery(id+"F12.wireOp",EDGE,"E3.top")])]});
            var sketch = newSketch(context, id + "F51", { "sketchPlane" : qUnion([Q0])});
            skLineSegment(sketch, "E7.bottom", {"start": v(589.75, 222.6) * mm, "end": v(-1340.65, 222.6) * mm});
            skLineSegment(sketch, "E7.top", {"start": v(589.75, -2020.49) * mm, "end": v(-1340.65, -2020.49) * mm});
            skLineSegment(sketch, "E7.left", {"start": v(589.75, 222.6) * mm, "end": v(589.75, -2020.49) * mm});
            skLineSegment(sketch, "E7.right", {"start": v(-1340.65, 222.6) * mm, "end": v(-1340.65, -2020.49) * mm});
            skSolve(sketch);
        }
        {
            var Q0;
            Q0 = qSketchRegion(id + "F51", true);
            extrude(context, id + "F52", {"entities" : qUnion([Q0]), "depth" : 25.4 * mm, "offsetDistance" : 25.4 * mm});
        }
        {
            var Q0;
            Q0=makeQuery(id+"F24.opExtrude","SWEPT_FACE",FACE,{"disambiguationData":[OSD([sQuery(id+"F23.wireOp",EDGE,"E4.top")])]});
            var sketch = newSketch(context, id + "F53", { "sketchPlane" : qUnion([Q0])});
            skLineSegment(sketch, "E8.bottom", {"start": v(-1359.08, -2016.26) * mm, "end": v(1386.21, -2016.26) * mm});
            skLineSegment(sketch, "E8.top", {"start": v(-1359.08, 0) * mm, "end": v(1386.21, 0) * mm});
            skLineSegment(sketch, "E8.left", {"start": v(-1359.08, -2016.26) * mm, "end": v(-1359.08, 0) * mm});
            skLineSegment(sketch, "E8.right", {"start": v(1386.21, -2016.26) * mm, "end": v(1386.21, 0) * mm});
            skSolve(sketch);
        }
        {
            var Q0;
            Q0 = qSketchRegion(id + "F53", true);
            extrude(context, id + "F54", {"entities" : qUnion([Q0]), "depth" : 25.4 * mm, "offsetDistance" : 25.4 * mm});
        }
        {
            var Q0;
            Q0=makeQuery(id+"F40.opPattern","COPY",BODY,{"derivedFrom":makeQuery(id+"F28.opExtrude","SWEPT_BODY",BODY,{"disambiguationData":[OSD([sQuery(id+"F27.wireOp",EDGE,"E5.bottom"),sQuery(id+"F27.wireOp",EDGE,"E5.top"),sQuery(id+"F27.wireOp",EDGE,"E5.left"),sQuery(id+"F27.wireOp",EDGE,"E5.right")])]}),"instanceName":"1"});
            transform(context, id + "F55", {"entities" : qUnion([Q0]), "transformType" : TransformType.TRANSLATION_3D, "dx" : -25.4 * mm, "dy" : 0 * mm, "dz" : 0 * mm, "makeCopy" : false});
        }
        {
            var Q0;
            Q0=makeQuery(id+"F1.opExtrude","SWEPT_BODY",BODY,{"disambiguationData":[OSD([sQuery(id+"F0.wireOp",EDGE,"E0.bottom"),sQuery(id+"F0.wireOp",EDGE,"E0.top"),sQuery(id+"F0.wireOp",EDGE,"E0.left"),sQuery(id+"F0.wireOp",EDGE,"E0.right")])]});
            var Q1;
            Q1=makeQuery(id+"F8.opPattern","COPY",BODY,{"derivedFrom":makeQuery(id+"F1.opExtrude","SWEPT_BODY",BODY,{"disambiguationData":[OSD([sQuery(id+"F0.wireOp",EDGE,"E0.bottom"),sQuery(id+"F0.wireOp",EDGE,"E0.top"),sQuery(id+"F0.wireOp",EDGE,"E0.left"),sQuery(id+"F0.wireOp",EDGE,"E0.right")])]}),"instanceName":"1"});
            var Q2;
            Q2=makeQuery(id+"F37.opExtrude","SWEPT_BODY",BODY,{"disambiguationData":[OSD([sQuery(id+"F36.wireOp",EDGE,"E6.bottom"),sQuery(id+"F36.wireOp",EDGE,"E6.top"),sQuery(id+"F36.wireOp",EDGE,"E6.left"),sQuery(id+"F36.wireOp",EDGE,"E6.right")])]});
            transform(context, id + "F56", {"entities" : qUnion([Q0, Q1, Q2]), "transformType" : TransformType.TRANSLATION_3D, "dx" : 0 * mm, "dy" : -222.25 * mm, "dz" : 0 * mm, "makeCopy" : false});
        }
        {
            var Q0;
            Q0=makeQuery(id+"F28.opExtrude","SWEPT_BODY",BODY,{"disambiguationData":[OSD([sQuery(id+"F27.wireOp",EDGE,"E5.bottom"),sQuery(id+"F27.wireOp",EDGE,"E5.top"),sQuery(id+"F27.wireOp",EDGE,"E5.left"),sQuery(id+"F27.wireOp",EDGE,"E5.right")])]});
            var Q1;
            Q1=makeQuery(id+"F1.opExtrude","SWEPT_BODY",BODY,{"disambiguationData":[OSD([sQuery(id+"F0.wireOp",EDGE,"E0.bottom"),sQuery(id+"F0.wireOp",EDGE,"E0.top"),sQuery(id+"F0.wireOp",EDGE,"E0.left"),sQuery(id+"F0.wireOp",EDGE,"E0.right")])]});
            var Q2;
            Q2=makeQuery(id+"F11.opPattern","COPY",BODY,{"derivedFrom":makeQuery(id+"F1.opExtrude","SWEPT_BODY",BODY,{"disambiguationData":[OSD([sQuery(id+"F0.wireOp",EDGE,"E0.bottom"),sQuery(id+"F0.wireOp",EDGE,"E0.top"),sQuery(id+"F0.wireOp",EDGE,"E0.left"),sQuery(id+"F0.wireOp",EDGE,"E0.right")])]}),"instanceName":"1"});
            transform(context, id + "F57", {"entities" : qUnion([Q0, Q1, Q2]), "transformType" : TransformType.TRANSLATION_3D, "dx" : 88.9 * mm, "dy" : 0 * mm, "dz" : 0 * mm, "makeCopy" : false});
        }
        {
            var Q0;
            Q0=makeQuery(id+"F8.opPattern","COPY",BODY,{"derivedFrom":makeQuery(id+"F1.opExtrude","SWEPT_BODY",BODY,{"disambiguationData":[OSD([sQuery(id+"F0.wireOp",EDGE,"E0.bottom"),sQuery(id+"F0.wireOp",EDGE,"E0.top"),sQuery(id+"F0.wireOp",EDGE,"E0.left"),sQuery(id+"F0.wireOp",EDGE,"E0.right")])]}),"instanceName":"1"});
            var Q1;
            Q1=makeQuery(id+"F10.opPattern","COPY",BODY,{"derivedFrom":makeQuery(id+"F8.opPattern","COPY",BODY,{"derivedFrom":makeQuery(id+"F1.opExtrude","SWEPT_BODY",BODY,{"disambiguationData":[OSD([sQuery(id+"F0.wireOp",EDGE,"E0.bottom"),sQuery(id+"F0.wireOp",EDGE,"E0.top"),sQuery(id+"F0.wireOp",EDGE,"E0.left"),sQuery(id+"F0.wireOp",EDGE,"E0.right")])]}),"instanceName":"1"}),"instanceName":"1"});
            var Q2;
            Q2=makeQuery(id+"F35.opPattern","COPY",BODY,{"derivedFrom":makeQuery(id+"F28.opExtrude","SWEPT_BODY",BODY,{"disambiguationData":[OSD([sQuery(id+"F27.wireOp",EDGE,"E5.bottom"),sQuery(id+"F27.wireOp",EDGE,"E5.top"),sQuery(id+"F27.wireOp",EDGE,"E5.left"),sQuery(id+"F27.wireOp",EDGE,"E5.right")])]}),"instanceName":"1"});
            transform(context, id + "F58", {"entities" : qUnion([Q0, Q1, Q2]), "transformType" : TransformType.TRANSLATION_3D, "dx" : -88.9 * mm, "dy" : 0 * mm, "dz" : 0 * mm, "makeCopy" : false});
        }
        {
            var Q0;
            Q0=makeQuery(id+"F13.opExtrude","SWEPT_FACE",FACE,{"disambiguationData":[OSD([sQuery(id+"F12.wireOp",EDGE,"E3.bottom")])]});
            var sketch = newSketch(context, id + "F59", { "sketchPlane" : qUnion([Q0])});
            skLineSegment(sketch, "E9.bottom", {"start": v(1336.89, 229.31) * mm, "end": v(-1108.83, 229.31) * mm});
            skLineSegment(sketch, "E9.top", {"start": v(1336.89, -2027.8) * mm, "end": v(-1108.83, -2027.8) * mm});
            skLineSegment(sketch, "E9.left", {"start": v(1336.89, 229.31) * mm, "end": v(1336.89, -2027.8) * mm});
            skLineSegment(sketch, "E9.right", {"start": v(-1108.83, 229.31) * mm, "end": v(-1108.83, -2027.8) * mm});
            skSolve(sketch);
        }
        {
            var Q0;
            Q0 = qSketchRegion(id + "F59", true);
            extrude(context, id + "F60", {"entities" : qUnion([Q0]), "depth" : 25.4 * mm, "offsetDistance" : 25.4 * mm});
        }
        {
            var Q0;
            Q0=makeQuery(id+"F24.opExtrude","SWEPT_FACE",FACE,{"disambiguationData":[OSD([sQuery(id+"F23.wireOp",EDGE,"E4.bottom")])]});
            var sketch = newSketch(context, id + "F61", { "sketchPlane" : qUnion([Q0])});
            skLineSegment(sketch, "E10.bottom", {"start": v(1380.66, 226.22) * mm, "end": v(1073.15, 226.22) * mm});
            skLineSegment(sketch, "E10.top", {"start": v(1380.66, -2018.52) * mm, "end": v(1073.15, -2018.52) * mm});
            skLineSegment(sketch, "E10.left", {"start": v(1380.66, 226.22) * mm, "end": v(1380.66, -2018.52) * mm});
            skLineSegment(sketch, "E10.right", {"start": v(1073.15, 226.22) * mm, "end": v(1073.15, -2018.52) * mm});
            skSolve(sketch);
        }
        {
            var Q0;
            Q0 = qSketchRegion(id + "F61", true);
            extrude(context, id + "F62", {"entities" : qUnion([Q0]), "depth" : 25.4 * mm, "offsetDistance" : 25.4 * mm});
        }
        {
            var Q0;
            Q0=makeQuery(id+"F24.opExtrude","SWEPT_FACE",FACE,{"disambiguationData":[OSD([sQuery(id+"F23.wireOp",EDGE,"E4.bottom")])]});
            var sketch = newSketch(context, id + "F63", { "sketchPlane" : qUnion([Q0])});
            skLineSegment(sketch, "E11.bottom", {"start": v(-1414.44, 229.31) * mm, "end": v(-1073.15, 229.31) * mm});
            skLineSegment(sketch, "E11.top", {"start": v(-1414.44, -2018.52) * mm, "end": v(-1073.15, -2018.52) * mm});
            skLineSegment(sketch, "E11.left", {"start": v(-1414.44, 229.31) * mm, "end": v(-1414.44, -2018.52) * mm});
            skLineSegment(sketch, "E11.right", {"start": v(-1073.15, 229.31) * mm, "end": v(-1073.15, -2018.52) * mm});
            skSolve(sketch);
        }
        {
            var Q0;
            Q0 = qSketchRegion(id + "F63", true);
            extrude(context, id + "F64", {"entities" : qUnion([Q0]), "depth" : 25.4 * mm, "offsetDistance" : 25.4 * mm});
        }
        {
            var Q0;
            Q0=makeQuery(id+"F13.opExtrude","SWEPT_FACE",FACE,{"disambiguationData":[OSD([sQuery(id+"F12.wireOp",EDGE,"E3.right")])]});
            var sketch = newSketch(context, id + "F65", { "sketchPlane" : qUnion([Q0])});
            skLineSegment(sketch, "E12.bottom", {"start": v(-1074.33, 232.4) * mm, "end": v(1074.56, 232.4) * mm});
            skLineSegment(sketch, "E12.top", {"start": v(-1074.33, -95.34) * mm, "end": v(1074.56, -95.34) * mm});
            skLineSegment(sketch, "E12.left", {"start": v(-1074.33, 232.4) * mm, "end": v(-1074.33, -95.34) * mm});
            skLineSegment(sketch, "E12.right", {"start": v(1074.56, 232.4) * mm, "end": v(1074.56, -95.34) * mm});
            skSolve(sketch);
        }
        {
            var Q0;
            Q0 = qSketchRegion(id + "F65", true);
            extrude(context, id + "F66", {"entities" : qUnion([Q0]), "depth" : 25.4 * mm, "offsetDistance" : 25.4 * mm});
        }
        {
            var Q0;
            Q0=makeQuery(id+"F13.opExtrude","CAP_FACE",FACE,{"disambiguationData":[OSD([sQuery(id+"F12.wireOp",EDGE,"E3.bottom"),sQuery(id+"F12.wireOp",EDGE,"E3.top"),sQuery(id+"F12.wireOp",EDGE,"E3.left"),sQuery(id+"F12.wireOp",EDGE,"E3.right")])],"isStart":false});
            var sketch = newSketch(context, id + "F67", { "sketchPlane" : qUnion([Q0])});
            skLineSegment(sketch, "E13.bottom", {"start": v(1384.3, 695.98) * mm, "end": v(-647.7, 695.98) * mm});
            skLineSegment(sketch, "E13.top", {"start": v(1384.3, -828.02) * mm, "end": v(-647.7, -828.02) * mm});
            skLineSegment(sketch, "E13.left", {"start": v(1384.3, 695.98) * mm, "end": v(1384.3, -828.02) * mm});
            skLineSegment(sketch, "E13.right", {"start": v(-647.7, 695.98) * mm, "end": v(-647.7, -828.02) * mm});
            skSolve(sketch);
        }
        {
            var Q0;
            Q0=makeQuery(id+"F67.imprint","IMPRINT",FACE,{"disambiguationData":[TD([[makeQuery(id+"F67.imprint","IMPRINT",EDGE,{"derivedFrom":sQuery(id+"F67.wireOp",EDGE,"E13.bottom")}),1.0]])]});
            extrude(context, id + "F68", {"entities" : qUnion([Q0]), "depth" : 304.8 * mm, "offsetDistance" : 25.4 * mm});
        }
        {
            var Q0;
            Q0=makeQuery(id+"F68.opExtrude","CAP_FACE",FACE,{"disambiguationData":[OSD([sQuery(id+"F67.wireOp",EDGE,"E13.bottom"),sQuery(id+"F67.wireOp",EDGE,"E13.top"),sQuery(id+"F67.wireOp",EDGE,"E13.left"),sQuery(id+"F67.wireOp",EDGE,"E13.right")])],"isStart":false});
            var Q1;
            Q1=makeQuery(id+"F68.opExtrude","CAP_FACE",FACE,{"disambiguationData":[OSD([sQuery(id+"F67.wireOp",EDGE,"E13.bottom"),sQuery(id+"F67.wireOp",EDGE,"E13.top"),sQuery(id+"F67.wireOp",EDGE,"E13.left"),sQuery(id+"F67.wireOp",EDGE,"E13.right")])],"isStart":true});
            fillet(context, id + "F69", {"entities" : qUnion([Q0, Q1]), "radius" : 25.4 * mm, "tangentPropagation" : true, "allowEdgeOverflow" : false});
        }
        {
            var Q0;
            Q0=makeQuery(id+"F68.opExtrude","SWEPT_FACE",FACE,{"disambiguationData":[OSD([sQuery(id+"F67.wireOp",EDGE,"E13.bottom")])]});
            var Q1;
            Q1=makeQuery(id+"F68.opExtrude","SWEPT_FACE",FACE,{"disambiguationData":[OSD([sQuery(id+"F67.wireOp",EDGE,"E13.right")])]});
            var Q2;
            Q2=makeQuery(id+"F68.opExtrude","SWEPT_FACE",FACE,{"disambiguationData":[OSD([sQuery(id+"F67.wireOp",EDGE,"E13.top")])]});
            var Q3;
            Q3=makeQuery(id+"F68.opExtrude","SWEPT_FACE",FACE,{"disambiguationData":[OSD([sQuery(id+"F67.wireOp",EDGE,"E13.left")])]});
            fillet(context, id + "F70", {"entities" : qUnion([Q0, Q1, Q2, Q3]), "radius" : 25.4 * mm, "tangentPropagation" : true, "allowEdgeOverflow" : false});
        }
        {
            var Q0;
            Q0=makeQuery(id+"F68.opExtrude","SWEPT_BODY",BODY,{"disambiguationData":[OSD([sQuery(id+"F67.wireOp",EDGE,"E13.bottom"),sQuery(id+"F67.wireOp",EDGE,"E13.top"),sQuery(id+"F67.wireOp",EDGE,"E13.left"),sQuery(id+"F67.wireOp",EDGE,"E13.right")])]});
            transform(context, id + "F71", {"entities" : qUnion([Q0]), "transformType" : TransformType.TRANSLATION_3D, "dx" : -25.4 * mm, "dy" : 152.4 * mm, "dz" : 0 * mm, "makeCopy" : false});
        }
        {
            var Q0;
            Q0=makeQuery(id+"F1.opExtrude","SWEPT_BODY",BODY,{"disambiguationData":[OSD([sQuery(id+"F0.wireOp",EDGE,"E0.bottom"),sQuery(id+"F0.wireOp",EDGE,"E0.top"),sQuery(id+"F0.wireOp",EDGE,"E0.left"),sQuery(id+"F0.wireOp",EDGE,"E0.right")])]});
            var Q1;
            Q1=makeQuery(id+"F11.opPattern","COPY",BODY,{"derivedFrom":makeQuery(id+"F1.opExtrude","SWEPT_BODY",BODY,{"disambiguationData":[OSD([sQuery(id+"F0.wireOp",EDGE,"E0.bottom"),sQuery(id+"F0.wireOp",EDGE,"E0.top"),sQuery(id+"F0.wireOp",EDGE,"E0.left"),sQuery(id+"F0.wireOp",EDGE,"E0.right")])]}),"instanceName":"1"});
            var Q2;
            Q2=makeQuery(id+"F28.opExtrude","SWEPT_BODY",BODY,{"disambiguationData":[OSD([sQuery(id+"F27.wireOp",EDGE,"E5.bottom"),sQuery(id+"F27.wireOp",EDGE,"E5.top"),sQuery(id+"F27.wireOp",EDGE,"E5.left"),sQuery(id+"F27.wireOp",EDGE,"E5.right")])]});
            transform(context, id + "F72", {"entities" : qUnion([Q0, Q1, Q2]), "transformType" : TransformType.TRANSLATION_3D, "dx" : -285.75 * mm, "dy" : 0 * mm, "dz" : 0 * mm, "makeCopy" : false});
        }
        {
            var Q0;
            Q0=makeQuery(id+"F8.opPattern","COPY",BODY,{"derivedFrom":makeQuery(id+"F1.opExtrude","SWEPT_BODY",BODY,{"disambiguationData":[OSD([sQuery(id+"F0.wireOp",EDGE,"E0.bottom"),sQuery(id+"F0.wireOp",EDGE,"E0.top"),sQuery(id+"F0.wireOp",EDGE,"E0.left"),sQuery(id+"F0.wireOp",EDGE,"E0.right")])]}),"instanceName":"1"});
            var Q1;
            Q1=makeQuery(id+"F10.opPattern","COPY",BODY,{"derivedFrom":makeQuery(id+"F8.opPattern","COPY",BODY,{"derivedFrom":makeQuery(id+"F1.opExtrude","SWEPT_BODY",BODY,{"disambiguationData":[OSD([sQuery(id+"F0.wireOp",EDGE,"E0.bottom"),sQuery(id+"F0.wireOp",EDGE,"E0.top"),sQuery(id+"F0.wireOp",EDGE,"E0.left"),sQuery(id+"F0.wireOp",EDGE,"E0.right")])]}),"instanceName":"1"}),"instanceName":"1"});
            var Q2;
            Q2=makeQuery(id+"F35.opPattern","COPY",BODY,{"derivedFrom":makeQuery(id+"F28.opExtrude","SWEPT_BODY",BODY,{"disambiguationData":[OSD([sQuery(id+"F27.wireOp",EDGE,"E5.bottom"),sQuery(id+"F27.wireOp",EDGE,"E5.top"),sQuery(id+"F27.wireOp",EDGE,"E5.left"),sQuery(id+"F27.wireOp",EDGE,"E5.right")])]}),"instanceName":"1"});
            transform(context, id + "F73", {"entities" : qUnion([Q0, Q1, Q2]), "transformType" : TransformType.TRANSLATION_3D, "dx" : 311.27 * mm, "dy" : 0 * mm, "dz" : 0 * mm, "makeCopy" : false});
        }
        {
            var Q0;
            Q0=makeQuery(id+"F40.opPattern","COPY",BODY,{"derivedFrom":makeQuery(id+"F28.opExtrude","SWEPT_BODY",BODY,{"disambiguationData":[OSD([sQuery(id+"F27.wireOp",EDGE,"E5.bottom"),sQuery(id+"F27.wireOp",EDGE,"E5.top"),sQuery(id+"F27.wireOp",EDGE,"E5.left"),sQuery(id+"F27.wireOp",EDGE,"E5.right")])]}),"instanceName":"1"});
            var Q1;
            Q1=makeQuery(id+"F52.opExtrude","CAP_EDGE",EDGE,{"disambiguationData":[OSD([sQuery(id+"F51.wireOp",EDGE,"E7.left")])],"isStart":false});
            transform(context, id + "F74", {"entities" : qUnion([Q0]), "transformType" : TransformType.ROTATION, "transformAxis" : qUnion([Q1]), "angle" : 90 * degree, "makeCopy" : false});
        }
        {
            var Q0;
            Q0=makeQuery(id+"F40.opPattern","COPY",BODY,{"derivedFrom":makeQuery(id+"F28.opExtrude","SWEPT_BODY",BODY,{"disambiguationData":[OSD([sQuery(id+"F27.wireOp",EDGE,"E5.bottom"),sQuery(id+"F27.wireOp",EDGE,"E5.top"),sQuery(id+"F27.wireOp",EDGE,"E5.left"),sQuery(id+"F27.wireOp",EDGE,"E5.right")])]}),"instanceName":"1"});
            transform(context, id + "F75", {"entities" : qUnion([Q0]), "transformType" : TransformType.TRANSLATION_3D, "dx" : 0 * mm, "dy" : -381 * mm, "dz" : 0 * mm, "makeCopy" : false});
        }
        {
            var Q0;
            Q0=makeQuery(id+"F13.opExtrude","SWEPT_FACE",FACE,{"disambiguationData":[OSD([sQuery(id+"F12.wireOp",EDGE,"E3.top")])]});
            var sketch = newSketch(context, id + "F76", { "sketchPlane" : qUnion([Q0])});
            skLineSegment(sketch, "E14.bottom", {"start": v(592, 226.67) * mm, "end": v(1107.17, 226.67) * mm});
            skLineSegment(sketch, "E14.top", {"start": v(592, -2019.92) * mm, "end": v(1107.17, -2019.92) * mm});
            skLineSegment(sketch, "E14.left", {"start": v(592, 226.67) * mm, "end": v(592, -2019.92) * mm});
            skLineSegment(sketch, "E14.right", {"start": v(1107.17, 226.67) * mm, "end": v(1107.17, -2019.92) * mm});
            skSolve(sketch);
        }
        {
            var Q0;
            Q0 = qSketchRegion(id + "F76", true);
            extrude(context, id + "F77", {"entities" : qUnion([Q0]), "depth" : 25.4 * mm, "offsetDistance" : 25.4 * mm});
        }
        {
            var Q0;
            Q0=makeQuery(id+"F13.opExtrude","SWEPT_FACE",FACE,{"disambiguationData":[OSD([sQuery(id+"F12.wireOp",EDGE,"E3.bottom")])]});
            var sketch = newSketch(context, id + "F78", { "sketchPlane" : qUnion([Q0])});
            skLineSegment(sketch, "E15.bottom", {"start": v(1336.88, 231.07) * mm, "end": v(-589.64, 231.07) * mm});
            skLineSegment(sketch, "E15.top", {"start": v(1336.88, -2017.84) * mm, "end": v(-589.64, -2017.84) * mm});
            skLineSegment(sketch, "E15.left", {"start": v(1336.88, 231.07) * mm, "end": v(1336.88, -2017.84) * mm});
            skLineSegment(sketch, "E15.right", {"start": v(-589.64, 231.07) * mm, "end": v(-589.64, -2017.84) * mm});
            skSolve(sketch);
        }
        {
            var Q0;
            Q0 = qSketchRegion(id + "F78", true);
            extrude(context, id + "F79", {"entities" : qUnion([Q0]), "depth" : 25.4 * mm, "offsetDistance" : 25.4 * mm});
        }
        {
            var Q0;
            Q0=makeQuery(id+"F68.opExtrude","SWEPT_BODY",BODY,{"disambiguationData":[OSD([sQuery(id+"F67.wireOp",EDGE,"E13.bottom"),sQuery(id+"F67.wireOp",EDGE,"E13.top"),sQuery(id+"F67.wireOp",EDGE,"E13.left"),sQuery(id+"F67.wireOp",EDGE,"E13.right")])]});
            transform(context, id + "F80", {"entities" : qUnion([Q0]), "transformType" : TransformType.TRANSLATION_3D, "dx" : 0 * mm, "dy" : 203.2 * mm, "dz" : 0 * mm, "makeCopy" : false});
        }
    });
